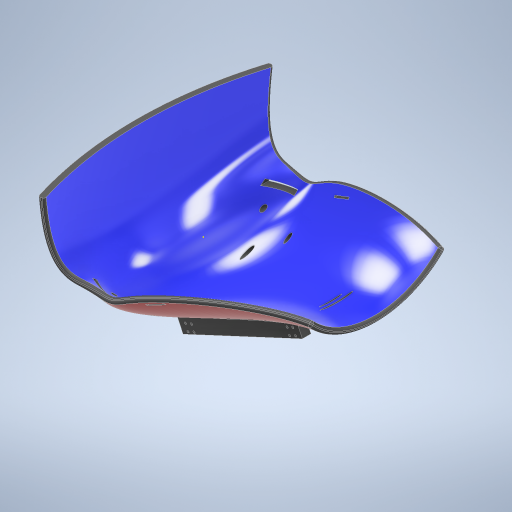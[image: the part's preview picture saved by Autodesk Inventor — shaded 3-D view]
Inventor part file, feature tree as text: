
AUTODESK INVENTOR PART (.ipt)
format: ipt  version: 2024 (Build 280153000, 153)  size: 1,643,008 bytes
history: native  units: in
note: dims shown in document units (in); Inventor stores cm internally (conversion verified against a paired STEP export)
features: sketch x3, extrude x2
ambient origin geometry x8: Origin, YZ Plane, XZ Plane, XY Plane, X Axis, Y Axis, Z Axis, Center Point
bodies: Solid1 (feature_tree), Body1 (feature_tree)
feature tree (5):
  extrude  "Extrusion1"  Depth=0.1969in
  extrude  "Extrusion2"  Depth=0.5906in
  sketch  "Sketch3"  dims[d4=0.5906in d5=0.5906in d6=0.1969in d7=0.5906in d8=0.1969in d9=0.1969in d10=0.5906in d11=0.1969in d12=0.1969in d13=0.5906in d14=0.1969in d15=0.5906in d16=0.1969in d17=0.1969in d18=0.5906in d19=0.5906in d20=22.6875in d21=0.0in d22=0.7874in d23=0.7874in d24=0.5512in d25=0.0in d26=0.5in d27=1.9685in]
  sketch  "Sketch1"  dims[d0=0.1969in d1=0.1969in]
  sketch  "Sketch2"  dims[d2=0.1969in d3=0.5906in]
